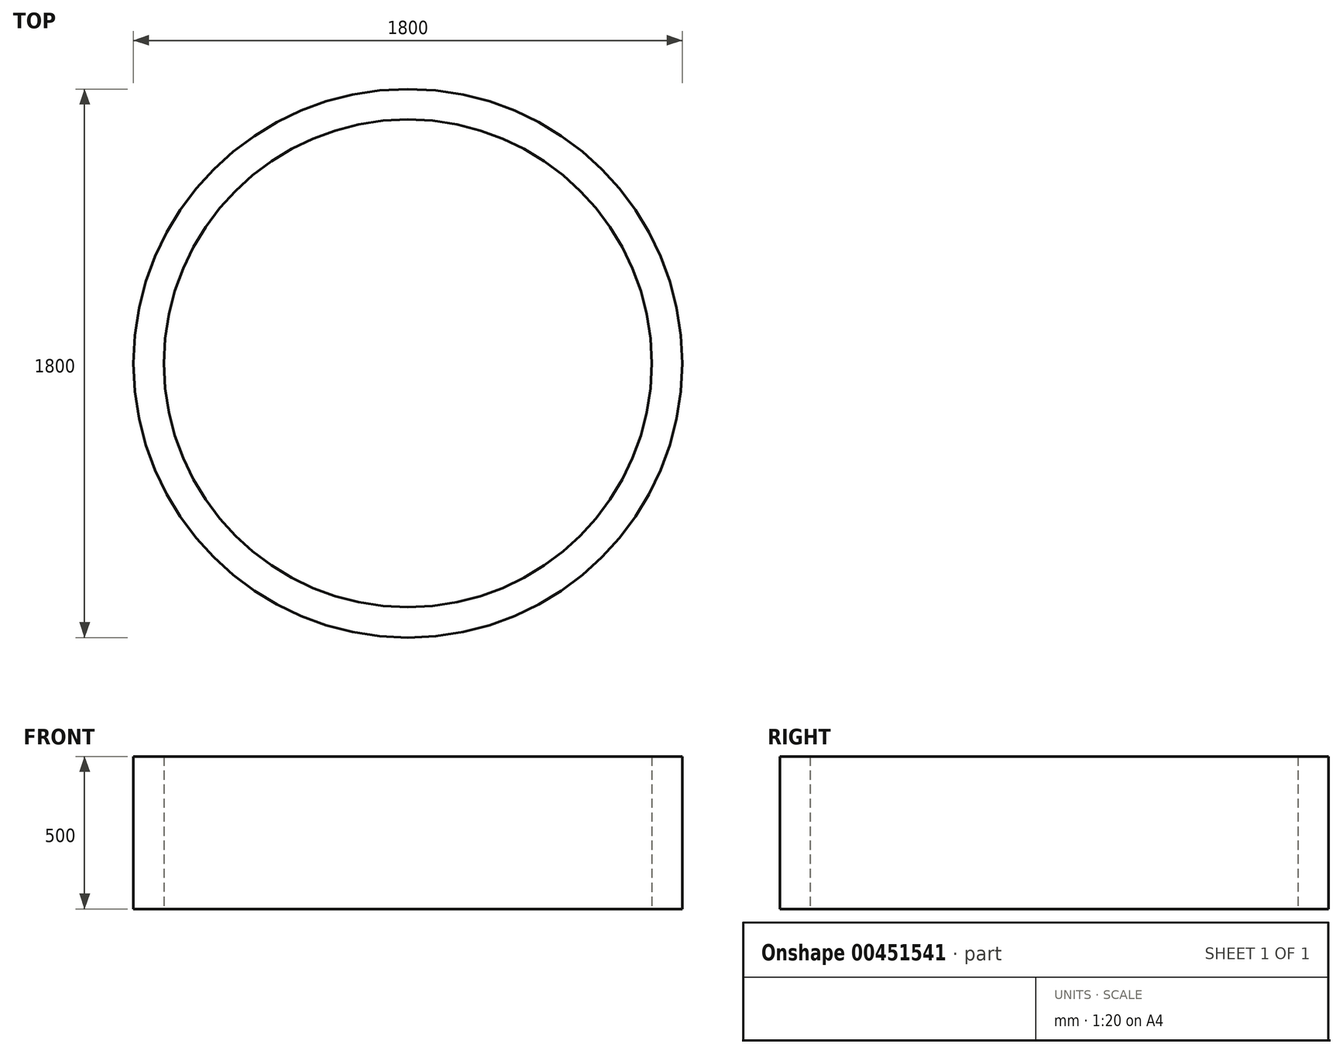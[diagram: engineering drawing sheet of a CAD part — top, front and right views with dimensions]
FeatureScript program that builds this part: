
annotation { "Feature Type Name" : "Feature", "Feature Type Description" : "" }
export const myFeature = defineFeature(function(context is Context, id is Id, definition is map)
    precondition{}
    {
        {
            var Q0;
            Q0=qCreatedBy(makeId("Top.planeOp"),FACE);
            var sketch = newSketch(context, id + "F0", { "sketchPlane" : qUnion([Q0])});
            skCircle(sketch, "E0", {"center": v(0, 0) * mm, "radius": 900 * mm});
            skCircle(sketch, "E1", {"center": v(0, 0) * mm, "radius": 800 * mm});
            skSolve(sketch);
        }
        {
            var Q0;
            Q0=makeQuery(id+"F0.imprint","IMPRINT",FACE,{"disambiguationData":[TD([[makeQuery(id+"F0.imprint","IMPRINT",EDGE,{"derivedFrom":sQuery(id+"F0.wireOp",EDGE,"E0")}),1.0]])]});
            extrude(context, id + "F1", {"entities" : qUnion([Q0]), "endBound" : BoundingType.SYMMETRIC, "depth" : 500 * mm});
        }
    });
